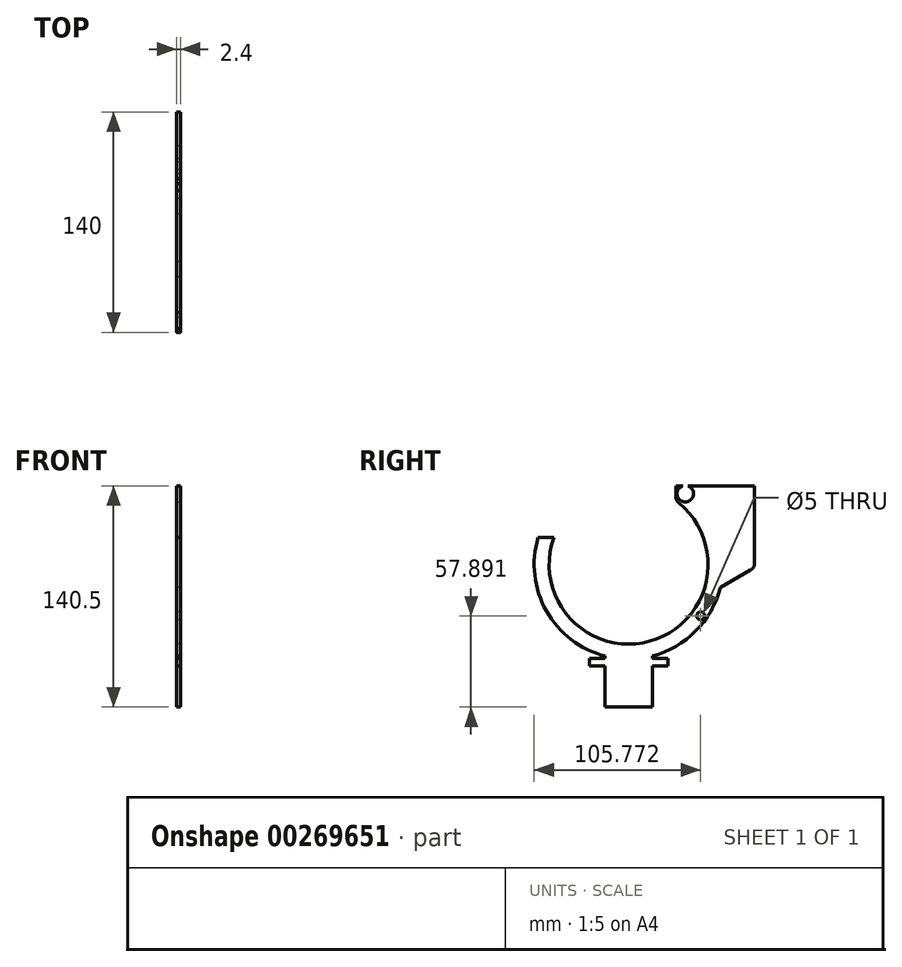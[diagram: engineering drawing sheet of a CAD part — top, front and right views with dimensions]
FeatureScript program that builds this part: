
annotation { "Feature Type Name" : "Feature", "Feature Type Description" : "" }
export const myFeature = defineFeature(function(context is Context, id is Id, definition is map)
    precondition{}
    {
        {
            var Q0;
            Q0=qCreatedBy(makeId("Right.planeOp"),FACE);
            var sketch = newSketch(context, id + "F0", { "sketchPlane" : qUnion([Q0])});
            skLineSegment(sketch, "E0", {"start": v(50, -52.08) * mm, "end": v(50, 0) * mm});
            skLineSegment(sketch, "E1", {"start": v(50, 0) * mm, "end": v(0, 0) * mm});
            skArc(sketch, "E2", {"start": v(-77.52, -32.91) * mm, "mid": v(-15.33, -98.32) * mm, "end": v(0, -9.38) * mm});
            skLineSegment(sketch, "E3", {"start": v(0, 0) * mm, "end": v(0, -9.38) * mm});
            skLineSegment(sketch, "E4", {"start": v(50, -52.08) * mm, "end": v(28.18, -64.68) * mm});
            skCircle(sketch, "E5", {"center": v(-30, -50) * mm, "radius": 50.5 * mm, "construction": true});
            skLineSegment(sketch, "E6", {"start": v(-77.52, -32.91) * mm, "end": v(-87.52, -32.91) * mm});
            skLineSegment(sketch, "E7", {"start": v(-15, -140.5) * mm, "end": v(-15, -108.1) * mm});
            skLineSegment(sketch, "E8", {"start": v(-45, -108.1) * mm, "end": v(-45, -140.5) * mm});
            skLineSegment(sketch, "E9", {"start": v(-45, -140.5) * mm, "end": v(-15, -140.5) * mm});
            skArc(sketch, "E10", {"start": v(-15, -108.1) * mm, "mid": v(12.54, -92.3) * mm, "end": v(28.18, -64.68) * mm});
            skArc(sketch, "E11.trimOffspring", {"start": v(-87.52, -32.91) * mm, "mid": v(-82.23, -79.54) * mm, "end": v(-45, -108.1) * mm});
            skLineSegment(sketch, "E12", {"start": v(-30, -50) * mm, "end": v(-30, -129.79) * mm, "construction": true});
            skSolve(sketch);
        }
        {
            var Q0;
            Q0=qSketchRegion(id+"F0",true);
            extrude(context, id + "F1", {"entities" : qUnion([Q0]), "depth" : 34 * mm});
        }
        {
            var Q0;
            Q0=makeQuery(id+"F1.opExtrude","SWEPT_EDGE",EDGE,{"disambiguationData":[OSD([sQuery(id+"F0.wireOp",EDGE,"E0"),sQuery(id+"F0.wireOp",EDGE,"E4")])]});
            var Q1;
            Q1=makeQuery(id+"F1.opExtrude","SWEPT_EDGE",EDGE,{"disambiguationData":[OSD([sQuery(id+"F0.wireOp",EDGE,"E2"),sQuery(id+"F0.wireOp",EDGE,"E3")])]});
            fillet(context, id + "F2", {"entities" : qUnion([Q0, Q1]), "radius" : 5 * mm, "tangentPropagation" : true, "allowEdgeOverflow" : false});
        }
        {
            var Q0;
            Q0=makeQuery(id+"F1.opExtrude","SWEPT_FACE",FACE,{"disambiguationData":[OSD([sQuery(id+"F0.wireOp",EDGE,"E1")])]});
            var Q1;
            Q1=makeQuery(id+"F1.opExtrude","SWEPT_FACE",FACE,{"disambiguationData":[OSD([sQuery(id+"F0.wireOp",EDGE,"E2")])]});
            var Q2;
            Q2=makeQuery(id+"F2.opFillet","BLEND_FACE",FACE,{"disambiguationData":[OSD([sQuery(id+"F0.wireOp",EDGE,"E2"),sQuery(id+"F0.wireOp",EDGE,"E3")])]});
            var Q3;
            Q3=makeQuery(id+"F1.opExtrude","SWEPT_FACE",FACE,{"disambiguationData":[OSD([sQuery(id+"F0.wireOp",EDGE,"E3")])]});
            var Q4;
            Q4=makeQuery(id+"F1.opExtrude","SWEPT_FACE",FACE,{"disambiguationData":[OSD([sQuery(id+"F0.wireOp",EDGE,"E6")])]});
            var Q5;
            Q5=makeQuery(id+"F1.opExtrude","SWEPT_FACE",FACE,{"disambiguationData":[OSD([sQuery(id+"F0.wireOp",EDGE,"E9")])]});
            shell(context, id + "F3", {"entities" : qUnion([Q0, Q1, Q2, Q3, Q4, Q5]), "thickness" : 2.4 * mm});
        }
        {
            var Q0;
            Q0=makeQuery(id+"F1.opExtrude","CAP_FACE",FACE,{"disambiguationData":[OSD([sQuery(id+"F0.wireOp",EDGE,"E0"),sQuery(id+"F0.wireOp",EDGE,"E1"),sQuery(id+"F0.wireOp",EDGE,"E2"),sQuery(id+"F0.wireOp",EDGE,"E3"),sQuery(id+"F0.wireOp",EDGE,"E4"),sQuery(id+"F0.wireOp",EDGE,"E6"),sQuery(id+"F0.wireOp",EDGE,"E7"),sQuery(id+"F0.wireOp",EDGE,"E8"),sQuery(id+"F0.wireOp",EDGE,"E9"),sQuery(id+"F0.wireOp",EDGE,"E10"),sQuery(id+"F0.wireOp",EDGE,"E11.trimOffspring")])],"isStart":false});
            var sketch = newSketch(context, id + "F4", { "sketchPlane" : qUnion([Q0])});
            skArc(sketch, "E13.0", {"start": v(-17.9, -99.03) * mm, "mid": v(3.32, -87.94) * mm, "end": v(17.06, -68.32) * mm, "construction": true});
            skArc(sketch, "E14", {"start": v(-17.9, -108.77) * mm, "mid": v(12.64, -92.2) * mm, "end": v(28.89, -61.5) * mm});
            skPoint(sketch, "E15.orphan", {"position": v(1.85, -10.8) * mm});
            skArc(sketch, "E16", {"start": v(-77.52, -32.91) * mm, "mid": v(-47.7, -97.3) * mm, "end": v(17.06, -68.32) * mm});
            skLineSegment(sketch, "E17.0", {"start": v(28.89, -61.5) * mm, "end": v(17.06, -68.32) * mm});
            skPoint(sketch, "E18.orphan", {"position": v(26.09, -63.11) * mm});
            skPoint(sketch, "E19.orphan", {"position": v(-17.4, -106.2) * mm});
            skPoint(sketch, "E20.orphan", {"position": v(46.3, -51.44) * mm});
            skPoint(sketch, "E21.orphan", {"position": v(28.18, -64.68) * mm});
            skPoint(sketch, "E22.orphan", {"position": v(-15, -108.1) * mm});
            skLineSegment(sketch, "E23", {"start": v(-17.9, -99.03) * mm, "end": v(-17.9, -108.77) * mm});
            skSolve(sketch);
        }
        {
            var Q0;
            Q0=qSketchRegion(id+"F4",true);
            var Q1;
            {var subQ0=sQuery(id+"F0.wireOp",EDGE,"E11.trimOffspring");var subQ1=sQuery(id+"F0.wireOp",EDGE,"E10");var subQ2=sQuery(id+"F0.wireOp",EDGE,"E9");var subQ3=sQuery(id+"F0.wireOp",EDGE,"E8");var subQ4=sQuery(id+"F0.wireOp",EDGE,"E7");var subQ5=sQuery(id+"F0.wireOp",EDGE,"E6");var subQ6=sQuery(id+"F0.wireOp",EDGE,"E4");var subQ7=sQuery(id+"F0.wireOp",EDGE,"E3");var subQ8=sQuery(id+"F0.wireOp",EDGE,"E2");var subQ9=sQuery(id+"F0.wireOp",EDGE,"E1");var subQ10=sQuery(id+"F0.wireOp",EDGE,"E0");Q1=makeQuery(id+"F3.opShell","OFFSET_FACE",FACE,{"disambiguationData":[OSD([subQ10,subQ9,subQ8,subQ7,subQ6,subQ5,subQ4,subQ3,subQ2,subQ1,subQ0]),TDD([makeQuery(id+"F1.opExtrude","CAP_FACE",FACE,{"disambiguationData":[OSD([subQ10,subQ9,subQ8,subQ7,subQ6,subQ5,subQ4,subQ3,subQ2,subQ1,subQ0])],"isStart":true})])]});}
            extrude(context, id + "F5", {"entities" : qUnion([Q0]), "operationType" : NewBodyOperationType.ADD, "endBound" : BoundingType.UP_TO_SURFACE, "oppositeDirection" : true, "endBoundEntityFace" : qUnion([Q1]), "depth" : 25 * mm});
        }
        {
            var Q0;
            Q0=makeQuery(id+"F1.opExtrude","CAP_FACE",FACE,{"disambiguationData":[OSD([sQuery(id+"F0.wireOp",EDGE,"E0"),sQuery(id+"F0.wireOp",EDGE,"E1"),sQuery(id+"F0.wireOp",EDGE,"E2"),sQuery(id+"F0.wireOp",EDGE,"E3"),sQuery(id+"F0.wireOp",EDGE,"E4")])],"isStart":true});
            var sketch = newSketch(context, id + "F6", { "sketchPlane" : qUnion([Q0])});
            skCircle(sketch, "E24", {"center": v(-6, -5) * mm, "radius": 2.5 * mm});
            skCircle(sketch, "E25", {"center": v(-15.77, -82.6) * mm, "radius": 2.5 * mm});
            skArc(sketch, "E26.0", {"start": v(77.52, -32.91) * mm, "mid": v(16.45, -98.65) * mm, "end": v(-1.85, -10.8) * mm, "construction": true});
            skLineSegment(sketch, "E27", {"start": v(30, -50) * mm, "end": v(-6, -5) * mm, "construction": true});
            skLineSegment(sketch, "E28", {"start": v(30, -50) * mm, "end": v(-15.77, -82.6) * mm, "construction": true});
            skLineSegment(sketch, "E29", {"start": v(-6, -5) * mm, "end": v(-15.77, -82.6) * mm, "construction": true});
            skSolve(sketch);
        }
        {
            var Q0;
            Q0=qSketchRegion(id+"F6",true);
            var Q1;
            Q1=makeQuery(id+"F1.opExtrude","CAP_FACE",FACE,{"disambiguationData":[OSD([sQuery(id+"F0.wireOp",EDGE,"E0"),sQuery(id+"F0.wireOp",EDGE,"E1"),sQuery(id+"F0.wireOp",EDGE,"E2"),sQuery(id+"F0.wireOp",EDGE,"E3"),sQuery(id+"F0.wireOp",EDGE,"E4"),sQuery(id+"F0.wireOp",EDGE,"E6"),sQuery(id+"F0.wireOp",EDGE,"E7"),sQuery(id+"F0.wireOp",EDGE,"E8"),sQuery(id+"F0.wireOp",EDGE,"E9"),sQuery(id+"F0.wireOp",EDGE,"E10"),sQuery(id+"F0.wireOp",EDGE,"E11.trimOffspring")])],"isStart":true});
            extrude(context, id + "F7", {"entities" : qUnion([Q0]), "operationType" : NewBodyOperationType.REMOVE, "endBound" : BoundingType.THROUGH_ALL, "oppositeDirection" : true, "endBoundEntityFace" : qUnion([Q1]), "depth" : 25 * mm});
        }
        {
            var Q0;
            Q0=makeQuery(id+"F5.opExtrude","SWEPT_EDGE",EDGE,{"disambiguationData":[OSD([sQuery(id+"F4.wireOp",EDGE,"E16"),sQuery(id+"F4.wireOp",EDGE,"E23")])]});
            fillet(context, id + "F8", {"entities" : qUnion([Q0]), "radius" : 5 * mm, "tangentPropagation" : true, "allowEdgeOverflow" : false});
        }
        {
            var Q0;
            Q0=makeQuery(id+"F1.opExtrude","SWEPT_FACE",FACE,{"disambiguationData":[OSD([sQuery(id+"F0.wireOp",EDGE,"E10")])]});
            shell(context, id + "F9", {"entities" : qUnion([Q0]), "thickness" : 2.4 * mm});
        }
        {
            var Q0;
            {var subQ0=sQuery(id+"F0.wireOp",EDGE,"E4");var subQ1=sQuery(id+"F0.wireOp",EDGE,"E0");var subQ2=sQuery(id+"F0.wireOp",EDGE,"E3");var subQ3=sQuery(id+"F0.wireOp",EDGE,"E2");var subQ4=sQuery(id+"F0.wireOp",EDGE,"E1");var subQ5=sQuery(id+"F0.wireOp",EDGE,"E11.trimOffspring");var subQ6=sQuery(id+"F0.wireOp",EDGE,"E10");var subQ7=sQuery(id+"F0.wireOp",EDGE,"E9");var subQ8=sQuery(id+"F0.wireOp",EDGE,"E8");var subQ9=sQuery(id+"F0.wireOp",EDGE,"E7");var subQ10=sQuery(id+"F0.wireOp",EDGE,"E6");Q0=makeQuery(id+"F5.boolean.opBoolean","SPLIT",FACE,{"disambiguationData":[TD([makeQuery(id+"F1.opExtrude","SWEPT_FACE",FACE,{"disambiguationData":[OSD([subQ4])]})])],"derivedFrom":makeQuery(id+"F3.opShell","OFFSET_FACE",FACE,{"disambiguationData":[OSD([subQ1,subQ4,subQ3,subQ2,subQ0,subQ10,subQ9,subQ8,subQ7,subQ6,subQ5]),TDD([makeQuery(id+"F1.opExtrude","CAP_FACE",FACE,{"disambiguationData":[OSD([subQ1,subQ4,subQ3,subQ2,subQ0,subQ10,subQ9,subQ8,subQ7,subQ6,subQ5])],"isStart":true})])]})});}
            cPlane(context, id + "F10", {"entities" : qUnion([Q0]), "cplaneType" : CPlaneType.OFFSET, "offset" : 7 * mm, "width" : 150 * mm, "height" : 150 * mm});
        }
        {
            var Q0;
            Q0=qCreatedBy(id+"F10.planeOp",FACE);
            var sketch = newSketch(context, id + "F11", { "sketchPlane" : qUnion([Q0])});
            skLineSegment(sketch, "E30.0", {"start": v(47.6, 0) * mm, "end": v(0, 0) * mm});
            skLineSegment(sketch, "E31.0", {"start": v(47.6, -49.19) * mm, "end": v(47.6, 0) * mm});
            skArc(sketch, "E32.0", {"start": v(47.6, -49.19) * mm, "mid": v(47.25, -50.49) * mm, "end": v(46.3, -51.44) * mm});
            skLineSegment(sketch, "E33.0", {"start": v(46.3, -51.44) * mm, "end": v(17.06, -68.32) * mm});
            skArc(sketch, "E34.0", {"start": v(17.06, -68.32) * mm, "mid": v(18.82, -37.09) * mm, "end": v(1.85, -10.8) * mm});
            skArc(sketch, "E35.0", {"start": v(1.85, -10.8) * mm, "mid": v(0.49, -9.08) * mm, "end": v(0, -6.93) * mm});
            skLineSegment(sketch, "E36.0", {"start": v(0, 0) * mm, "end": v(0, -6.93) * mm});
            skCircle(sketch, "E37.0", {"center": v(6, -5) * mm, "radius": 2.5 * mm});
            skSolve(sketch);
        }
        {
            var Q0;
            Q0=qSketchRegion(id+"F11",true);
            extrude(context, id + "F12", {"entities" : qUnion([Q0]), "operationType" : NewBodyOperationType.ADD, "depth" : 4 * mm});
        }
        {
            var Q0;
            Q0=makeQuery(id+"F6.imprint","IMPRINT",FACE,{"disambiguationData":[TD([[makeQuery(id+"F6.imprint","IMPRINT",EDGE,{"derivedFrom":sQuery(id+"F6.wireOp",EDGE,"E24")}),-1.0]])]});
            var sketch = newSketch(context, id + "F13", { "sketchPlane" : qUnion([Q0])});
            skCircle(sketch, "E38.0", {"center": v(-6, -5) * mm, "radius": 2.5 * mm});
            skCircle(sketch, "E39", {"center": v(-6, -5) * mm, "radius": 5 * mm});
            skSolve(sketch);
        }
        {
            var Q0;
            Q0=qSketchRegion(id+"F13",true);
            var Q1;
            {var subQ0=sQuery(id+"F0.wireOp",EDGE,"E4");var subQ1=sQuery(id+"F0.wireOp",EDGE,"E0");var subQ2=sQuery(id+"F0.wireOp",EDGE,"E3");var subQ3=sQuery(id+"F0.wireOp",EDGE,"E2");var subQ4=sQuery(id+"F0.wireOp",EDGE,"E1");var subQ5=sQuery(id+"F0.wireOp",EDGE,"E11.trimOffspring");var subQ6=sQuery(id+"F0.wireOp",EDGE,"E10");var subQ7=sQuery(id+"F0.wireOp",EDGE,"E9");var subQ8=sQuery(id+"F0.wireOp",EDGE,"E8");var subQ9=sQuery(id+"F0.wireOp",EDGE,"E7");var subQ10=sQuery(id+"F0.wireOp",EDGE,"E6");Q1=makeQuery(id+"F5.boolean.opBoolean","SPLIT",FACE,{"disambiguationData":[TD([makeQuery(id+"F1.opExtrude","SWEPT_FACE",FACE,{"disambiguationData":[OSD([subQ4])]})])],"derivedFrom":makeQuery(id+"F3.opShell","OFFSET_FACE",FACE,{"disambiguationData":[OSD([subQ1,subQ4,subQ3,subQ2,subQ0,subQ10,subQ9,subQ8,subQ7,subQ6,subQ5]),TDD([makeQuery(id+"F1.opExtrude","CAP_FACE",FACE,{"disambiguationData":[OSD([subQ1,subQ4,subQ3,subQ2,subQ0,subQ10,subQ9,subQ8,subQ7,subQ6,subQ5])],"isStart":false})])]})});}
            extrude(context, id + "F14", {"entities" : qUnion([Q0]), "operationType" : NewBodyOperationType.ADD, "endBound" : BoundingType.UP_TO_SURFACE, "oppositeDirection" : true, "endBoundEntityFace" : qUnion([Q1]), "depth" : 25 * mm});
        }
        {
            var Q0;
            Q0=makeQuery(id+"F6.imprint","IMPRINT",FACE,{"disambiguationData":[TD([[makeQuery(id+"F6.imprint","IMPRINT",EDGE,{"derivedFrom":sQuery(id+"F6.wireOp",EDGE,"E24")}),-1.0]])]});
            var sketch = newSketch(context, id + "F15", { "sketchPlane" : qUnion([Q0])});
            skLineSegment(sketch, "E40.0", {"start": v(45, -109.49) * mm, "end": v(45, -114.49) * mm});
            skLineSegment(sketch, "E41.0", {"start": v(15, -114.49) * mm, "end": v(15, -109.49) * mm});
            skLineSegment(sketch, "E42.bottom", {"start": v(5, -109.49) * mm, "end": v(15, -109.49) * mm});
            skLineSegment(sketch, "E42.top", {"start": v(5, -114.49) * mm, "end": v(15, -114.49) * mm});
            skLineSegment(sketch, "E42.left", {"start": v(5, -109.49) * mm, "end": v(5, -114.49) * mm});
            skLineSegment(sketch, "E42.right", {"start": v(55, -109.49) * mm, "end": v(55, -114.49) * mm});
            skLineSegment(sketch, "E43.trimOffspring", {"start": v(45, -109.49) * mm, "end": v(55, -109.49) * mm});
            skLineSegment(sketch, "E44.trimOffspring", {"start": v(45, -114.49) * mm, "end": v(55, -114.49) * mm});
            skPoint(sketch, "E45.orphan", {"position": v(15, -140.5) * mm});
            skPoint(sketch, "E46.orphan", {"position": v(45, -140.5) * mm});
            skPoint(sketch, "E47.orphan", {"position": v(45, -108.1) * mm});
            skPoint(sketch, "E48.orphan", {"position": v(15, -108.1) * mm});
            skSolve(sketch);
        }
        {
            var Q0;
            Q0=qSketchRegion(id+"F15",true);
            var Q1;
            Q1=makeQuery(id+"F1.opExtrude","CAP_FACE",FACE,{"disambiguationData":[OSD([sQuery(id+"F0.wireOp",EDGE,"E0"),sQuery(id+"F0.wireOp",EDGE,"E1"),sQuery(id+"F0.wireOp",EDGE,"E2"),sQuery(id+"F0.wireOp",EDGE,"E3"),sQuery(id+"F0.wireOp",EDGE,"E4"),sQuery(id+"F0.wireOp",EDGE,"E6"),sQuery(id+"F0.wireOp",EDGE,"E7"),sQuery(id+"F0.wireOp",EDGE,"E8"),sQuery(id+"F0.wireOp",EDGE,"E9"),sQuery(id+"F0.wireOp",EDGE,"E10"),sQuery(id+"F0.wireOp",EDGE,"E11.trimOffspring")])],"isStart":false});
            extrude(context, id + "F16", {"entities" : qUnion([Q0]), "operationType" : NewBodyOperationType.ADD, "endBound" : BoundingType.UP_TO_SURFACE, "oppositeDirection" : true, "endBoundEntityFace" : qUnion([Q1]), "depth" : 25 * mm});
        }
        {
            var Q0;
            {var subQ2=sQuery(id+"F0.wireOp",EDGE,"E9");var subQ5=sQuery(id+"F0.wireOp",EDGE,"E8");Q0=makeQuery(id+"F16.boolean.opBoolean","SPLIT",FACE,{"disambiguationData":[TD([makeQuery(id+"F1.opExtrude","SWEPT_FACE",FACE,{"disambiguationData":[OSD([subQ2])]})])],"derivedFrom":makeQuery(id+"F1.opExtrude","SWEPT_FACE",FACE,{"disambiguationData":[OSD([subQ5])]})});}
            var sketch = newSketch(context, id + "F17", { "sketchPlane" : qUnion([Q0])});
            skLineSegment(sketch, "E49", {"start": v(0, -127.5) * mm, "end": v(34, -127.5) * mm, "construction": true});
            skLineSegment(sketch, "E50", {"start": v(17, -140.5) * mm, "end": v(17, -114.49) * mm, "construction": true});
            skCircle(sketch, "E51", {"center": v(17, -127.5) * mm, "radius": 2.1 * mm});
            skSolve(sketch);
        }
        {
            var Q0;
            Q0=qSketchRegion(id+"F17",true);
            extrude(context, id + "F18", {"entities" : qUnion([Q0]), "operationType" : NewBodyOperationType.REMOVE, "endBound" : BoundingType.THROUGH_ALL, "oppositeDirection" : true, "depth" : 25 * mm});
        }
        {
            var Q0;
            {var subQ0=sQuery(id+"F0.wireOp",EDGE,"E4");var subQ1=sQuery(id+"F0.wireOp",EDGE,"E0");var subQ2=sQuery(id+"F0.wireOp",EDGE,"E3");var subQ3=sQuery(id+"F0.wireOp",EDGE,"E2");var subQ4=sQuery(id+"F0.wireOp",EDGE,"E1");var subQ5=sQuery(id+"F0.wireOp",EDGE,"E11.trimOffspring");var subQ6=sQuery(id+"F0.wireOp",EDGE,"E10");var subQ7=sQuery(id+"F0.wireOp",EDGE,"E9");var subQ8=sQuery(id+"F0.wireOp",EDGE,"E8");var subQ9=sQuery(id+"F0.wireOp",EDGE,"E7");var subQ10=sQuery(id+"F0.wireOp",EDGE,"E6");Q0=makeQuery(id+"F5.boolean.opBoolean","SPLIT",FACE,{"disambiguationData":[TD([makeQuery(id+"F1.opExtrude","SWEPT_FACE",FACE,{"disambiguationData":[OSD([subQ4])]})])],"derivedFrom":makeQuery(id+"F3.opShell","OFFSET_FACE",FACE,{"disambiguationData":[OSD([subQ1,subQ4,subQ3,subQ2,subQ0,subQ10,subQ9,subQ8,subQ7,subQ6,subQ5]),TDD([makeQuery(id+"F1.opExtrude","CAP_FACE",FACE,{"disambiguationData":[OSD([subQ1,subQ4,subQ3,subQ2,subQ0,subQ10,subQ9,subQ8,subQ7,subQ6,subQ5])],"isStart":true})])]})});}
            var sketch = newSketch(context, id + "F19", { "sketchPlane" : qUnion([Q0])});
            skLineSegment(sketch, "E52.bottom", {"start": v(-117.95, 19.96) * mm, "end": v(69.12, 19.96) * mm});
            skLineSegment(sketch, "E52.top", {"start": v(-117.95, -154.51) * mm, "end": v(69.12, -154.51) * mm});
            skLineSegment(sketch, "E52.left", {"start": v(-117.95, 19.96) * mm, "end": v(-117.95, -154.51) * mm});
            skLineSegment(sketch, "E52.right", {"start": v(69.12, 19.96) * mm, "end": v(69.12, -154.51) * mm});
            skSolve(sketch);
        }
        {
            var Q0;
            Q0 = qSketchRegion(id + "F19", true);
            extrude(context, id + "F20", {"entities" : qUnion([Q0]), "operationType" : NewBodyOperationType.REMOVE, "endBound" : BoundingType.THROUGH_ALL, "depth" : 25 * mm});
        }
        {
            var Q0;
            {var subQ0=sQuery(id+"F0.wireOp",EDGE,"E4");var subQ1=sQuery(id+"F0.wireOp",EDGE,"E0");var subQ3=sQuery(id+"F0.wireOp",EDGE,"E3");var subQ4=sQuery(id+"F0.wireOp",EDGE,"E2");var subQ6=sQuery(id+"F0.wireOp",EDGE,"E1");var subQ8=sQuery(id+"F0.wireOp",EDGE,"E11.trimOffspring");var subQ9=sQuery(id+"F0.wireOp",EDGE,"E10");var subQ10=sQuery(id+"F0.wireOp",EDGE,"E9");var subQ11=sQuery(id+"F0.wireOp",EDGE,"E8");var subQ12=sQuery(id+"F0.wireOp",EDGE,"E7");var subQ13=sQuery(id+"F0.wireOp",EDGE,"E6");var subQ14=makeQuery(id+"F1.opExtrude","CAP_FACE",FACE,{"disambiguationData":[OSD([subQ1,subQ6,subQ4,subQ3,subQ0,subQ13,subQ12,subQ11,subQ10,subQ9,subQ8])],"isStart":true});var subQ15=makeQuery(id+"F3.opShell","OFFSET_FACE",FACE,{"disambiguationData":[OSD([subQ1,subQ6,subQ4,subQ3,subQ0,subQ13,subQ12,subQ11,subQ10,subQ9,subQ8]),TDD([subQ14])]});var subQ16=subQ14;Q0=makeQuery(id+"F20.boolean.opBoolean","MERGE",FACE,{"derivedFrom":[makeQuery(id+"F5.boolean.opBoolean","SPLIT",FACE,{"disambiguationData":[TD([makeQuery(id+"F1.opExtrude","SWEPT_FACE",FACE,{"disambiguationData":[OSD([subQ13])]})])],"derivedFrom":subQ15}),makeQuery(id+"F9.opShell","OFFSET_FACE",FACE,{"disambiguationData":[OSD([subQ1,subQ6,subQ4,subQ3,subQ0,subQ13,subQ12,subQ11,subQ10,subQ9,subQ8]),TDD([subQ16]),OD(0.0)]}),makeQuery(id+"F9.opShell","OFFSET_FACE",FACE,{"disambiguationData":[OSD([subQ1,subQ6,subQ4,subQ3,subQ0,subQ13,subQ12,subQ11,subQ10,subQ9,subQ8]),TDD([subQ16]),OD(1.0)]}),makeQuery(id+"F5.boolean.opBoolean","SPLIT",FACE,{"disambiguationData":[TD([makeQuery(id+"F1.opExtrude","SWEPT_FACE",FACE,{"disambiguationData":[OSD([subQ6])]})])],"derivedFrom":subQ15}),makeQuery(id+"F20.opExtrude","CAP_FACE",FACE,{"disambiguationData":[OSD([sQuery(id+"F19.wireOp",EDGE,"E52.bottom"),sQuery(id+"F19.wireOp",EDGE,"E52.top"),sQuery(id+"F19.wireOp",EDGE,"E52.left"),sQuery(id+"F19.wireOp",EDGE,"E52.right")])],"isStart":true})]});}
            var sketch = newSketch(context, id + "F21", { "sketchPlane" : qUnion([Q0])});
            skCircle(sketch, "E53", {"center": v(6, -5) * mm, "radius": 5.25 * mm});
            skSolve(sketch);
        }
        {
            var Q0;
            Q0 = qSketchRegion(id + "F21", true);
            extrude(context, id + "F22", {"entities" : qUnion([Q0]), "operationType" : NewBodyOperationType.REMOVE, "endBound" : BoundingType.THROUGH_ALL, "oppositeDirection" : true, "depth" : 25 * mm});
        }
    });
